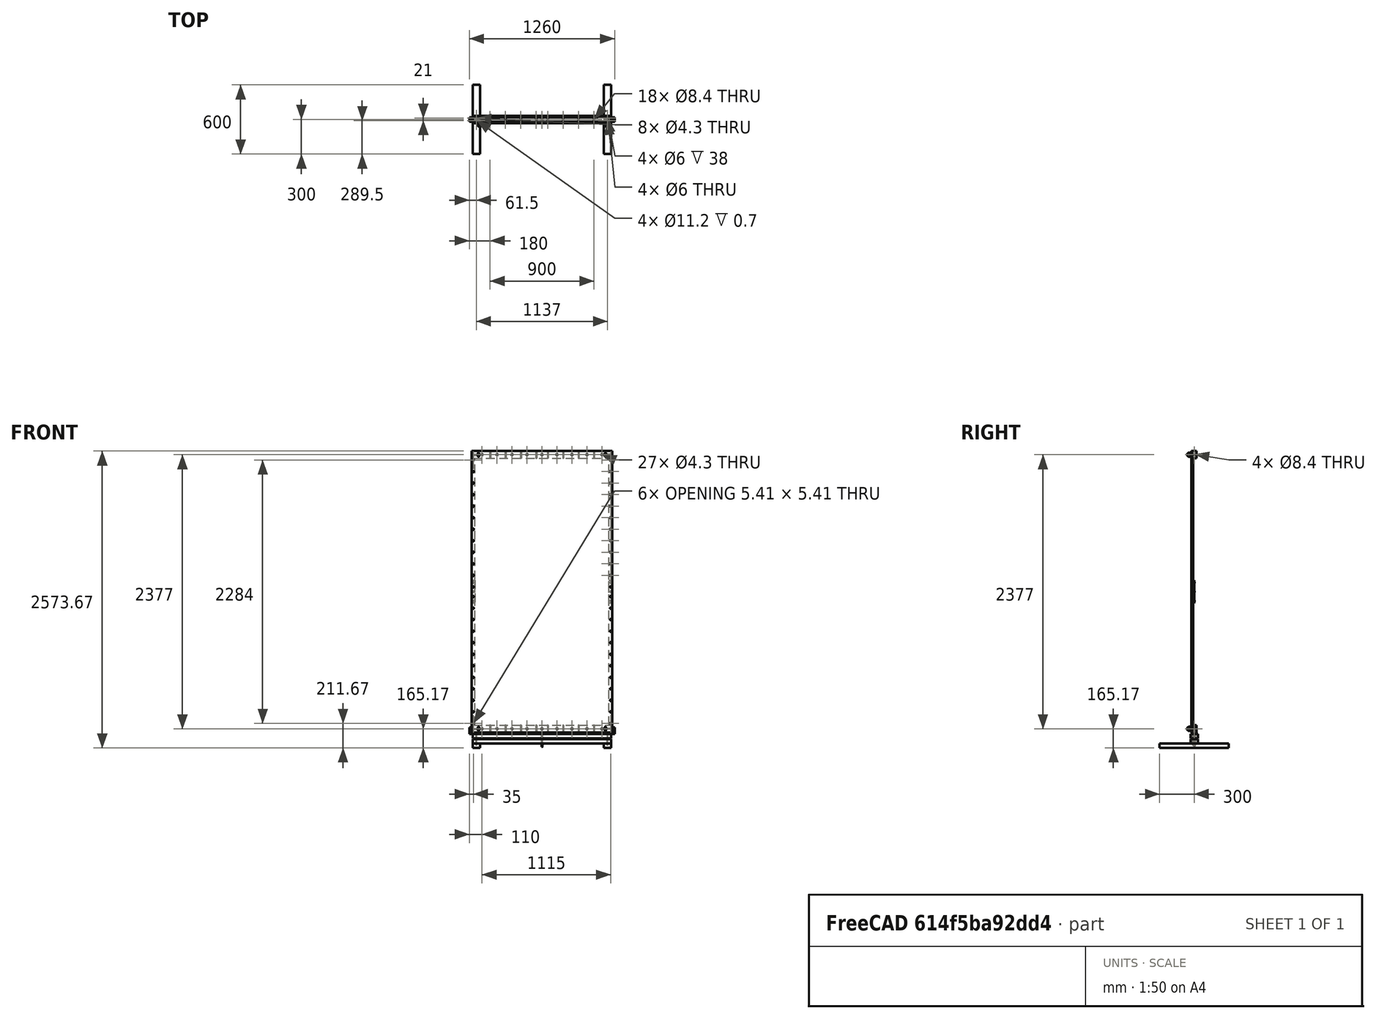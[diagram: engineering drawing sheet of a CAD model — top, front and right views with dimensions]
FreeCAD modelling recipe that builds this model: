
FCSTD DOCUMENT  (FreeCAD 0.21R33771 (Git))
Label: reflector_2024_assembly
License: All rights reserved
LicenseURL: https://en.wikipedia.org/wiki/All_rights_reserved
objects: Part::FeaturePython×30, Part::Compound×4, Part::Feature×4, Part::Mirroring×2, TechDraw::DrawSVGTemplate×1, TechDraw::DrawPage×1
note: 32 computed .brp shape members not serialized (recipe doc carries the construction recipe); baked Part::Feature solids carry a one-line shape summary decoded from their .brp

FEATURE [Part::FeaturePython] b_reflector_2024_panel_001_  label="panel"  # a2plus imported part (geometry in sourceFile) (typed FeaturePython)
  a2p_Version = 0.4.64
  fixedPosition = true
  objectType = a2pPart
  sourceFile = ./Assembly Parts/panel.FCStd
  sourcePart = panel
  subassemblyImport = false
  timeLastImport = 1.71105e+09
  updateColors = true
FEATURE [Part::FeaturePython] b_reflector_2024_listello_001_  label="strip_wood_001"  # a2plus imported part (geometry in sourceFile) (typed FeaturePython)
  Placement = pos=(-595,5,0) rot=(0,0,1;0rad)
  a2p_Version = 0.4.64
  fixedPosition = false
  objectType = a2pPart
  sourceFile = ./Assembly Parts/strip_wood.FCStd
  sourcePart = Body
  subassemblyImport = false
  timeLastImport = 1.71105e+09
  updateColors = true
  expr: .Placement.Base.x = -610 + 15
FEATURE [Part::FeaturePython] b_reflector_2024_listello_Body_001_  label="strip_wood_002"  # a2plus imported part (geometry in sourceFile) (typed FeaturePython)
  Placement = pos=(595,5,0) rot=(0,-1,0;0rad)
  a2p_Version = 0.4.64
  fixedPosition = false
  objectType = a2pPart
  sourceFile = ./Assembly Parts/strip_wood.FCStd
  sourcePart = Body
  subassemblyImport = false
  timeLastImport = 1.71105e+09
  updateColors = true
  expr: .Placement.Base.x = 610 - 15
FEATURE [Part::FeaturePython] Screw006  label="M6x12-Screw"  # Fasteners workbench fastener (typed FeaturePython)
  Placement = pos=(595,-6,1142) rot=(1,0,0;1.5708rad)
  diameter = 8
  invert = false
  leftHanded = false
  length = 2
  lengthCustom = 12
  matchOuter = false
  offset = 0
  thread = false
  type = 73
  expr: .Placement.Base.x = 1220 / 2 - 30 / 2
  expr: .Placement.Base.y = -6
  expr: .Placement.Base.z = 1220 - 63 - 15
FEATURE [Part::FeaturePython] Array004  # Draft array (typed FeaturePython)
  AlwaysSyncPlacement = false
  Angle = 360
  ArrayType = 0
  Axis = (0,0,1)
  Base = -> Screw006
  Center = (0,0,0)
  Count = 12
  ExpandArray = false
  Fuse = false
  IntervalAxis = (0,0,0)
  IntervalX = (100,0,0)
  IntervalY = (0,100,0)
  IntervalZ = (0,0,-100)
  NumberCircles = 3
  NumberPolar = 5
  NumberX = 1
  NumberY = 1
  NumberZ = 12
  PlacementList = 12 placements: arithmetic series from (595,-6,1142) step (0,0,-100) to (595,-6,42)
  RadialDistance = 50
  ScaleList = (12) [(1,1,1),(1,1,1),(1,1,1),(1,1,1),(1,1,1),(1,1,1),(1,1,1),(1,1,1),(1,1,1),(1,1,1),(1,1,1),(1,1,1)]
  Symmetry = 1
  TangentialDistance = 25
FEATURE [Part::FeaturePython] Screw007  label="M6x12-Screw001"  # Fasteners workbench fastener (typed FeaturePython)
  Placement = pos=(595,-6,-1142) rot=(1,0,0;1.5708rad)
  diameter = 8
  invert = false
  leftHanded = false
  length = 2
  lengthCustom = 12
  matchOuter = false
  offset = 0
  thread = false
  type = 73
  expr: .Placement.Base.x = 1220 / 2 - 30 / 2
  expr: .Placement.Base.y = -6
  expr: .Placement.Base.z = -(1220 - 63 - 15)
FEATURE [Part::FeaturePython] Array005  # Draft array (typed FeaturePython)
  AlwaysSyncPlacement = false
  Angle = 360
  ArrayType = 0
  Axis = (0,0,1)
  Base = -> Screw007
  Center = (0,0,0)
  Count = 12
  ExpandArray = false
  Fuse = false
  IntervalAxis = (0,0,0)
  IntervalX = (100,0,0)
  IntervalY = (0,100,0)
  IntervalZ = (0,0,100)
  NumberCircles = 3
  NumberPolar = 5
  NumberX = 1
  NumberY = 1
  NumberZ = 12
  PlacementList = 12 placements: arithmetic series from (595,-6,-1142) step (0,0,100) to (595,-6,-42)
  RadialDistance = 50
  ScaleList = (12) [(1,1,1),(1,1,1),(1,1,1),(1,1,1),(1,1,1),(1,1,1),(1,1,1),(1,1,1),(1,1,1),(1,1,1),(1,1,1),(1,1,1)]
  Symmetry = 1
  TangentialDistance = 25
FEATURE [Part::FeaturePython] Screw008  label="M6x12-Screw004"  # Fasteners workbench fastener (typed FeaturePython)
  Placement = pos=(-595,-6,1142) rot=(1,0,0;1.5708rad)
  diameter = 8
  invert = false
  leftHanded = false
  length = 2
  lengthCustom = 12
  matchOuter = false
  offset = 0
  thread = false
  type = 73
  expr: .Placement.Base.x = -(1220 / 2 - 30 / 2)
  expr: .Placement.Base.y = -6
  expr: .Placement.Base.z = 1220 - 63 - 15
FEATURE [Part::FeaturePython] Array006  # Draft array (typed FeaturePython)
  AlwaysSyncPlacement = false
  Angle = 360
  ArrayType = 0
  Axis = (0,0,1)
  Base = -> Screw008
  Center = (0,0,0)
  Count = 12
  ExpandArray = false
  Fuse = false
  IntervalAxis = (0,0,0)
  IntervalX = (100,0,0)
  IntervalY = (0,100,0)
  IntervalZ = (0,0,-100)
  NumberCircles = 3
  NumberPolar = 5
  NumberX = 1
  NumberY = 1
  NumberZ = 12
  PlacementList = 12 placements: arithmetic series from (-595,-6,1142) step (0,0,-100) to (-595,-6,42)
  RadialDistance = 50
  ScaleList = (12) [(1,1,1),(1,1,1),(1,1,1),(1,1,1),(1,1,1),(1,1,1),(1,1,1),(1,1,1),(1,1,1),(1,1,1),(1,1,1),(1,1,1)]
  Symmetry = 1
  TangentialDistance = 25
FEATURE [Part::FeaturePython] Screw009  label="M6x12-Screw005"  # Fasteners workbench fastener (typed FeaturePython)
  Placement = pos=(-595,-6,-1142) rot=(1,0,0;1.5708rad)
  diameter = 8
  invert = false
  leftHanded = false
  length = 2
  lengthCustom = 12
  matchOuter = false
  offset = 0
  thread = false
  type = 73
  expr: .Placement.Base.x = -(1220 / 2 - 30 / 2)
  expr: .Placement.Base.y = -6
  expr: .Placement.Base.z = -(1220 - 63 - 15)
FEATURE [Part::FeaturePython] Array007  # Draft array (typed FeaturePython)
  AlwaysSyncPlacement = false
  Angle = 360
  ArrayType = 0
  Axis = (0,0,1)
  Base = -> Screw009
  Center = (0,0,0)
  Count = 12
  ExpandArray = false
  Fuse = false
  IntervalAxis = (0,0,0)
  IntervalX = (100,0,0)
  IntervalY = (0,100,0)
  IntervalZ = (0,0,100)
  NumberCircles = 3
  NumberPolar = 5
  NumberX = 1
  NumberY = 1
  NumberZ = 12
  PlacementList = 12 placements: arithmetic series from (-595,-6,-1142) step (0,0,100) to (-595,-6,-42)
  RadialDistance = 50
  ScaleList = (12) [(1,1,1),(1,1,1),(1,1,1),(1,1,1),(1,1,1),(1,1,1),(1,1,1),(1,1,1),(1,1,1),(1,1,1),(1,1,1),(1,1,1)]
  Symmetry = 1
  TangentialDistance = 25
FEATURE [Part::FeaturePython] Screw010  label="M6x8-Screw"  # Fasteners workbench fastener (typed FeaturePython)
  Placement = pos=(0,-7,1188.5) rot=(1,0,0;1.5708rad)
  diameter = 8
  invert = false
  leftHanded = false
  length = 0
  lengthCustom = 8
  matchOuter = false
  offset = 0
  thread = false
  type = 73
FEATURE [Part::FeaturePython] Array  # Draft array (typed FeaturePython)
  AlwaysSyncPlacement = false
  Angle = 360
  ArrayType = 0
  Axis = (0,0,1)
  Base = -> Screw010
  Center = (0,0,0)
  Count = 5
  ExpandArray = false
  Fuse = false
  IntervalAxis = (0,0,0)
  IntervalX = (130,0,0)
  IntervalY = (0,100,0)
  IntervalZ = (0,0,100)
  NumberCircles = 3
  NumberPolar = 5
  NumberX = 5
  NumberY = 1
  NumberZ = 1
  PlacementList = 5 placements: arithmetic series from (0,-7,1188.5) step (130,0,0) to (520,-7,1188.5)
  RadialDistance = 50
  ScaleList = (5) [(1,1,1),(1,1,1),(1,1,1),(1,1,1),(1,1,1)]
  Symmetry = 1
  TangentialDistance = 25
FEATURE [Part::Compound] Compound001  label="screws_strips"
  Links = -> [Array004,Array005,Array006,Array007]
FEATURE [Part::FeaturePython] Array008  # Draft array (typed FeaturePython)
  AlwaysSyncPlacement = false
  Angle = 360
  ArrayType = 0
  Axis = (0,0,1)
  Base = -> Screw010
  Center = (0,0,0)
  Count = 5
  ExpandArray = false
  Fuse = false
  IntervalAxis = (0,0,0)
  IntervalX = (-130,0,0)
  IntervalY = (0,100,0)
  IntervalZ = (0,0,100)
  NumberCircles = 3
  NumberPolar = 5
  NumberX = 5
  NumberY = 1
  NumberZ = 1
  PlacementList = 5 placements: arithmetic series from (0,-7,1188.5) step (-130,0,0) to (-520,-7,1188.5)
  RadialDistance = 50
  ScaleList = (5) [(1,1,1),(1,1,1),(1,1,1),(1,1,1),(1,1,1)]
  Symmetry = 1
  TangentialDistance = 25
FEATURE [Part::FeaturePython] Screw011  label="M6x8-Screw011"  # Fasteners workbench fastener (typed FeaturePython)
  Placement = pos=(0,-7,-1188.5) rot=(1,0,0;1.5708rad)
  diameter = 8
  invert = false
  leftHanded = false
  length = 0
  lengthCustom = 8
  matchOuter = false
  offset = 0
  thread = false
  type = 73
  expr: .Placement.Base.z = -1188.5 mm
FEATURE [Part::FeaturePython] Array009  # Draft array (typed FeaturePython)
  AlwaysSyncPlacement = false
  Angle = 360
  ArrayType = 0
  Axis = (0,0,1)
  Base = -> Screw011
  Center = (0,0,0)
  Count = 5
  ExpandArray = false
  Fuse = false
  IntervalAxis = (0,0,0)
  IntervalX = (130,0,0)
  IntervalY = (0,100,0)
  IntervalZ = (0,0,100)
  NumberCircles = 3
  NumberPolar = 5
  NumberX = 5
  NumberY = 1
  NumberZ = 1
  PlacementList = 5 placements: arithmetic series from (0,-7,-1188.5) step (130,0,0) to (520,-7,-1188.5)
  RadialDistance = 50
  ScaleList = (5) [(1,1,1),(1,1,1),(1,1,1),(1,1,1),(1,1,1)]
  Symmetry = 1
  TangentialDistance = 25
FEATURE [Part::FeaturePython] Array010  # Draft array (typed FeaturePython)
  AlwaysSyncPlacement = false
  Angle = 360
  ArrayType = 0
  Axis = (0,0,1)
  Base = -> Screw011
  Center = (0,0,0)
  Count = 5
  ExpandArray = false
  Fuse = false
  IntervalAxis = (0,0,0)
  IntervalX = (-130,0,0)
  IntervalY = (0,100,0)
  IntervalZ = (0,0,100)
  NumberCircles = 3
  NumberPolar = 5
  NumberX = 5
  NumberY = 1
  NumberZ = 1
  PlacementList = 5 placements: arithmetic series from (0,-7,-1188.5) step (-130,0,0) to (-520,-7,-1188.5)
  RadialDistance = 50
  ScaleList = (5) [(1,1,1),(1,1,1),(1,1,1),(1,1,1),(1,1,1)]
  Symmetry = 1
  TangentialDistance = 25
FEATURE [Part::Compound] Compound  label="screws_battens"
  Links = -> [Array,Array008,Array009,Array010]
FEATURE [Part::Feature] Part__Feature  label="LIFTING EYE BOLT - M8 - DIN 580_1"
  Placement = pos=(550,-25,1188.5) rot=(0.707107,0,-0.707107;3.14159rad)
  shape: bbox 21.03 x 49.35 x 36.93 mm, 59 faces (baked)
  expr: .Placement.Base.x = 610 - 60
  expr: .Placement.Base.z = 1220 - 63 / 2
FEATURE [Part::Feature] Part__Feature001  label="LIFTING EYE BOLT - M8 - DIN 580_2"
  Placement = pos=(-550,-25,1188.5) rot=(0.707107,0,-0.707107;3.14159rad)
  shape: bbox 21.03 x 49.35 x 36.93 mm, 59 faces (baked)
  expr: .Placement.Base.x = -(610 - 60)
  expr: .Placement.Base.z = 1220 - 63 / 2
FEATURE [Part::Feature] Part__Feature002  label="LIFTING EYE BOLT - M8 - DIN 580_3"
  Placement = pos=(550,-25,-1188.5) rot=(0.707107,0,-0.707107;3.14159rad)
  shape: bbox 21.03 x 49.35 x 36.93 mm, 59 faces (baked)
  expr: .Placement.Base.x = 610 - 60
  expr: .Placement.Base.z = -(1220 - 63 / 2)
FEATURE [Part::Feature] Part__Feature003  label="LIFTING EYE BOLT - M8 - DIN 580_4"
  Placement = pos=(-550,-25,-1188.5) rot=(0.707107,0,-0.707107;3.14159rad)
  shape: bbox 21.03 x 49.35 x 36.93 mm, 59 faces (baked)
  expr: .Placement.Base.x = -(610 - 60)
  expr: .Placement.Base.z = -(1220 - 63 / 2)
FEATURE [Part::Compound] Compound002  label="eye_bolts"
  Links = -> [Part__Feature,Part__Feature001,Part__Feature002,Part__Feature003]
FEATURE [Part::FeaturePython] b_reflector_2024_listello_handle_001_  label="strip_wood_handle_001"  # a2plus imported part (geometry in sourceFile) (typed FeaturePython)
  Placement = pos=(595,20,0) rot=(0,0,1;0rad)
  a2p_Version = 0.4.64
  fixedPosition = false
  objectType = a2pPart
  sourceFile = ./Assembly Parts/strip_wood_handle.FCStd
  subassemblyImport = false
  timeLastImport = 1.71105e+09
  updateColors = true
  expr: .Placement.Base.x = 610 - 15
FEATURE [Part::FeaturePython] b_reflector_2024_listello_handle_001_001  label="strip_wood_handle_002"  # a2plus imported part (geometry in sourceFile) (typed FeaturePython)
  Placement = pos=(-595,20,0) rot=(0,0,1;0rad)
  a2p_Version = 0.4.64
  fixedPosition = false
  objectType = a2pPart
  sourceFile = ./Assembly Parts/strip_wood_handle.FCStd
  subassemblyImport = false
  timeLastImport = 1.71105e+09
  updateColors = true
  expr: .Placement.Base.x = -610 + 15
FEATURE [Part::FeaturePython] Screw  label="M6x25-Screw"  # Fasteners workbench fastener (typed FeaturePython)
  Placement = pos=(595,21,0) rot=(-1,0,0;1.5708rad)
  diameter = 8
  invert = false
  leftHanded = false
  length = 6
  lengthCustom = 25
  matchOuter = false
  offset = 0
  thread = false
  type = 73
  expr: .Placement.Base.x = 610 - 15
FEATURE [Part::FeaturePython] Screw012  label="M6x25-Screw001"  # Fasteners workbench fastener (typed FeaturePython)
  Placement = pos=(595,21,80) rot=(-1,0,0;1.5708rad)
  diameter = 8
  invert = false
  leftHanded = false
  length = 6
  lengthCustom = 25
  matchOuter = false
  offset = 0
  thread = false
  type = 73
  expr: .Placement.Base.x = 610 - 15
FEATURE [Part::FeaturePython] Screw013  label="M6x25-Screw002"  # Fasteners workbench fastener (typed FeaturePython)
  Placement = pos=(595,21,-80) rot=(-1,0,0;1.5708rad)
  diameter = 8
  invert = false
  leftHanded = false
  length = 6
  lengthCustom = 25
  matchOuter = false
  offset = 0
  thread = false
  type = 73
  expr: .Placement.Base.x = 610 - 15
FEATURE [Part::FeaturePython] Screw014  label="M6x25-Screw003"  # Fasteners workbench fastener (typed FeaturePython)
  Placement = pos=(-595,21,0) rot=(-1,0,0;1.5708rad)
  diameter = 8
  invert = false
  leftHanded = false
  length = 6
  lengthCustom = 25
  matchOuter = false
  offset = 0
  thread = false
  type = 73
  expr: .Placement.Base.x = -610 + 15
FEATURE [Part::FeaturePython] Screw015  label="M6x25-Screw004"  # Fasteners workbench fastener (typed FeaturePython)
  Placement = pos=(-595,21,80) rot=(-1,0,0;1.5708rad)
  diameter = 8
  invert = false
  leftHanded = false
  length = 6
  lengthCustom = 25
  matchOuter = false
  offset = 0
  thread = false
  type = 73
  expr: .Placement.Base.x = -610 + 15
FEATURE [Part::FeaturePython] Screw016  label="M6x25-Screw005"  # Fasteners workbench fastener (typed FeaturePython)
  Placement = pos=(-595,21,-80) rot=(-1,0,0;1.5708rad)
  diameter = 8
  invert = false
  leftHanded = false
  length = 6
  lengthCustom = 25
  matchOuter = false
  offset = 0
  thread = false
  type = 73
  expr: .Placement.Base.x = -610 + 15
FEATURE [Part::Compound] Compound003  label="screws_handles"
  Links = -> [Screw,Screw012,Screw013,Screw014,Screw015,Screw016]
FEATURE [Part::FeaturePython] b_reflector_2024_timber_001_  label="timber_batten_001"  # a2plus imported part (geometry in sourceFile) (typed FeaturePython)
  Placement = pos=(0,19,1188.5) rot=(0,0,1;0rad)
  a2p_Version = 0.4.64
  fixedPosition = false
  objectType = a2pPart
  sourceFile = ./Assembly Parts/timber_batten.FCStd
  subassemblyImport = false
  timeLastImport = 1.71105e+09
  updateColors = true
  expr: .Placement.Base.y = 38 / 2
FEATURE [Part::FeaturePython] b_reflector_2024_timber_001_001  label="timber_batten_002"  # a2plus imported part (geometry in sourceFile) (typed FeaturePython)
  Placement = pos=(0,19,-1188.5) rot=(0,0,1;0rad)
  a2p_Version = 0.4.64
  fixedPosition = false
  objectType = a2pPart
  sourceFile = ./Assembly Parts/timber_batten.FCStd
  subassemblyImport = false
  timeLastImport = 1.71105e+09
  updateColors = true
  expr: .Placement.Base.y = 38 / 2
FEATURE [TechDraw::DrawSVGTemplate] Template
  Height = 594
  Orientation = 1
  Template = /snap/freecad/908/usr/share/Mod/TechDraw/Templates/A1_Landscape_blank.svg
  Width = 841
FEATURE [TechDraw::DrawPage] Page
  KeepUpdated = true
  NextBalloonIndex = 1
  ProjectionType = 0
  Template = -> Template
FEATURE [Part::FeaturePython] ScrewTap  label="M8x35-ScrewTap"  # Fasteners workbench fastener (typed FeaturePython)
  Placement = pos=(622,19,-1188.5) rot=(0,1,0;1.5708rad)
  diameter = 9
  diameterCustom = 6
  invert = false
  leftHanded = false
  length = 35
  matchOuter = false
  offset = 0
  pitchCustom = 1
  thread = false
  type = 2
  expr: .Placement.Base.y = 38 / 2
  expr: .Placement.Base.z = -1220 + 63 / 2
FEATURE [Part::Mirroring] Mirror  label="M8x35-ScrewTap (mirrored)"
  Base = (0,0,0)
  Normal = (1,0,0)
  Source = -> ScrewTap
FEATURE [Part::FeaturePython] b_reflector_2024_base_001_  label="hypatia_base_001"  # a2plus imported part (geometry in sourceFile) (typed FeaturePython)
  Placement = pos=(0,19,-1296.67) rot=(0,0,1;0rad)
  a2p_Version = 0.4.64
  fixedPosition = false
  objectType = a2pPart
  sourceFile = ./hypatia_base.FCStd
  subassemblyImport = true
  timeLastImport = 1.71105e+09
  updateColors = true
FEATURE [Part::FeaturePython] Nut  label="M8-Nut"  # Fasteners workbench fastener (typed FeaturePython)
  Placement = pos=(612,19,-1188.5) rot=(0,1,0;1.5708rad)
  diameter = 3
  invert = false
  leftHanded = false
  matchOuter = false
  offset = 0
  thread = false
  type = 32
  expr: .Placement.Base.y = 38 / 2
  expr: .Placement.Base.z = -1220 + 63 / 2
FEATURE [Part::Mirroring] Mirror001  label="M8-Nut (mirrored)"
  Base = (0,0,0)
  Normal = (1,0,0)
  Source = -> Nut
